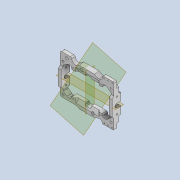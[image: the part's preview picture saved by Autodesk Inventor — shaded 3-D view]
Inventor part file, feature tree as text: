
AUTODESK INVENTOR PART (.ipt)
format: ipt  version: 2020 (Build 240168000, 168)  size: 971,776 bytes
history: native  units: mm
features: sketch x22, extrude x20, projected_geometry x20, reference x17, fillet x14, other x12, mirror x8, thicken_offset x8, plane x3, chamfer x3, hole x2
ambient origin geometry x8: Origin, YZ Plane, XZ Plane, XY Plane, X Axis, Y Axis, Z Axis, Center Point
bodies: Solid1 (feature_tree)
feature tree (129):
  extrude  "Extrusion1"  Depth=30.0mm
  extrude  "Extrusion2"  Depth=56.0mm
  plane  "Work Plane1"
  mirror  "Mirror1"
  extrude  "Extrusion3"  Depth=20.0mm
  extrude  "Extrusion4"  Depth=4.0mm TaperAngle=0.0deg
  plane  "Work Plane2"
  extrude  "Extrusion5"  Depth=10.0mm
  extrude  "Extrusion6"  Depth=1.5mm
  plane  "Work Plane3"
  mirror  "Mirror2"
  extrude  "Extrusion7"  Depth=80.0mm TaperAngle=0.0deg
  mirror  "Mirror3"
  fillet  "Fillet1"  Radius=3.0mm
  thicken_offset  "Thicken1"
  thicken_offset  "Thicken2"
  extrude  "Extrusion8"  Depth=6.0mm TaperAngle=0.0deg
  mirror  "Mirror4"
  extrude  "Extrusion10"  Depth=10.0mm
  thicken_offset  "Thicken3"
  mirror  "Mirror5"
  thicken_offset  "Thicken4"
  extrude  "Extrusion11"  Depth=3.5mm
  extrude  "Extrusion12"  Depth=10.0mm TaperAngle=0.0deg
  fillet  "Fillet4"  Radius=8.0mm
  extrude  "Extrusion13"  Depth=1.0mm
  extrude  "Extrusion14"  Depth=1.0mm
  extrude  "Extrusion15"  Depth=4.0mm
  extrude  "Extrusion16"  Depth=1.0mm
  thicken_offset  "Thicken5"
  fillet  "Fillet7"  Radius=1.5mm
  fillet  "Fillet8"  Radius=4.0mm
  fillet  "Fillet9"  Radius=3.0mm
  fillet  "Fillet10"  Radius=10.0mm
  fillet  "Fillet11"  Radius=4.0mm
  fillet  "Fillet12"  Radius=1.0mm
  extrude  "Extrusion17"  Depth=0.5mm
  mirror  "Mirror6"
  extrude  "Extrusion18"  Depth=10.0mm
  hole  "Hole1"  [1 undecoded]
  extrude  "Extrusion19"  Depth=2.8mm
  thicken_offset  "Thicken6"
  hole  "Hole2"  [1 undecoded]
  extrude  "Extrusion20"  Depth=6.0mm TaperAngle=0.0deg
  extrude  "Extrusion21"  Depth=1.0mm
  mirror  "Mirror7"
  fillet  "Fillet13"  Radius=6.0mm
  mirror  "Mirror8"
  fillet  "Fillet14"  Radius=15.0mm
  fillet  "Fillet15"  Radius=2.8mm
  chamfer  "Chamfer1"  Distance=6.0mm
  fillet  "Fillet16"  Radius=1.5mm
  chamfer  "Chamfer2"  Distance=1.5mm
  chamfer  "Chamfer3"  Distance=4.0mm
  fillet  "Fillet17"  Radius=3.0mm
  fillet  "Fillet18"  Radius=4.0mm
  thicken_offset  "Thicken7"
  thicken_offset  "Thicken8"
  sketch  "Sketch1"  dims[d0=50.0mm d1=30.0mm]
  reference  "Reference1"
  reference  "Reference2"
  sketch  "Sketch2"  dims[d2=36.0mm d3=56.0mm]
  projected_geometry  "Projected Loop1"
  reference  "Reference3"
  sketch  "Sketch3"  dims[d4=4.0mm d5=0.0mm d6=20.0mm]
  reference  "Reference4"
  sketch  "Sketch4"  dims[d7=8.0mm d8=4.0mm d9=0.0mm]
  reference  "Reference5"
  reference  "Reference6"
  sketch  "Sketch5"  dims[d10=10.0mm d11=4.0mm]
  projected_geometry  "Projected Loop2"
  projected_geometry  "Projected Loop3"
  projected_geometry  "Projected Loop4"
  reference  "Reference7"
  sketch  "Sketch6"  dims[d12=80.0mm d13=0.0mm d14=1.5mm]
  projected_geometry  "Projected Loop5"
  projected_geometry  "Projected Loop6"
  sketch  "Sketch7"  dims[d15=1.5mm d16=80.0mm d17=0.0mm d18=3.0mm]
  projected_geometry  "Projected Loop7"
  projected_geometry  "Projected Loop8"
  sketch  "Sketch8"  dims[d19=3.0mm d20=6.0mm d21=0.0mm]
  projected_geometry  "Projected Loop9"
  reference  "Reference8"
  reference  "Reference9"
  sketch  "Sketch10"  dims[d22=10.0mm d23=0.0mm d24=3.5mm]
  projected_geometry  "Projected Loop11"
  sketch  "Sketch11"  dims[d25=5.0mm d26=3.5mm]
  projected_geometry  "Projected Loop13"
  projected_geometry  "Projected Loop14"
  sketch  "Sketch12"  dims[d27=5.0mm d28=10.0mm d29=0.0mm d30=8.0mm]
  reference  "Reference11"
  sketch  "Sketch13"  dims[d32=1.0mm d33=1.0mm]
  projected_geometry  "Projected Loop15"
  sketch  "Sketch14"  dims[d34=1.0mm d35=1.0mm]
  projected_geometry  "Projected Loop16"
  sketch  "Sketch15"  dims[d36=1.5mm d37=4.0mm]
  projected_geometry  "Projected Loop17"
  sketch  "Sketch16"  dims[d38=3.0mm d39=2.0mm d40=1.5mm d41=4.0mm d42=3.0mm d43=10.0mm d44=0.0mm d49=4.0mm d50=0.0mm d51=0.5mm d52=1.0mm]
  reference  "Reference12"
  sketch  "Sketch17"  dims[d53=0.5mm d54=0.5mm]
  projected_geometry  "Projected Loop18"
  sketch  "Sketch18"  dims[d55=10.0mm d56=0.0mm d58=29.0mm]
  reference  "Reference13"
  reference  "Reference14"
  projected_geometry  "Projected Loop19"
  sketch  "Sketch19"  dims[d59=6.0mm d60=0.0mm d61=1.0mm]
  reference  "Reference15"
  sketch  "Sketch20"  dims[d63=2.0mm d64=2.8mm]
  reference  "Reference16"
  projected_geometry  "Projected Loop20"
  sketch  "Sketch21"  dims[d65=6.0mm d66=0.0mm d67=2.0mm]
  reference  "Reference17"
  sketch  "Sketch22"  dims[d68=2.8mm d69=6.0mm d70=0.0mm]
  projected_geometry  "Projected Loop21"
  reference  "Reference18"
  sketch  "Sketch23"  dims[d71=12.0mm d72=5.0mm d73=6.0mm d74=0.0mm d76=15.0mm d78=2.8mm d79=6.0mm d80=0.0mm d81=1.5mm d82=1.5mm d83=4.0mm d84=3.0mm d85=4.0mm d86=1.0mm d87=1.5mm d88=2.0mm d89=1.0mm d90=2.0mm d91=1.1mm d92=2.0mm d93=1.1mm d94=8.0mm d95=0.0mm d96=2.8mm d97=5.0mm d98=2.8mm d99=6.0mm d100=12.0mm d101=0.0mm d102=1.1mm d103=6.0mm d104=4.0mm d105=2.0mm d106=90.0deg d107=100.0mm d108=0.0mm d109=3.0mm d110=4.0mm d111=0.0mm d112=0.005mm d113=0.005mm d114=1.1mm d115=6.0mm d116=4.0mm d117=2.0mm d118=90.0deg d119=100.0mm d120=0.0mm d121=12.0mm d122=4.5mm d123=4.0mm d124=0.0mm d125=3.0mm d126=3.0mm d127=3.0mm d128=2.0mm d129=6.0mm d130=0.0mm d131=3.0mm d132=3.0mm d133=1.0mm d134=2.5mm d135=2.0mm d136=45.0deg d137=2.0mm d138=1.0mm d139=2.0mm d140=45.0deg d141=1.0mm d142=2.0mm d143=45.0deg d144=1.0mm d145=1.0mm d146=1.0mm d147=1.0mm d148=1.0mm d149=1.0mm]
  projected_geometry  "Projected Loop22"
  parser-record x1  (decoder bookkeeping rows leaked as tree rows — omitted from the tree; the rows remain in map.json)
  other  "tip_3_ass.iam"
  other  "bearing_hh_1:1"
  other  "bearing_hh_1:2"
  other  "pin_3_30:2"
  other  "roller_1:2"
  other  "roller_1:1"
  other  "c_roller_1:2"
  other  "c_roller_1:1"
  other  "bw_ass_1:1"
  other  "bw_hl_1:1"
  other  "bw_ass_1:2"
note: 2 required parameter values undecoded (feature->parameter linkage not recoverable at this tier; creation-order binding heuristic only, values carry confidence <= 0.55)
note: 1 file-system path scrubbed to <path> (originals preserved in map.json)
